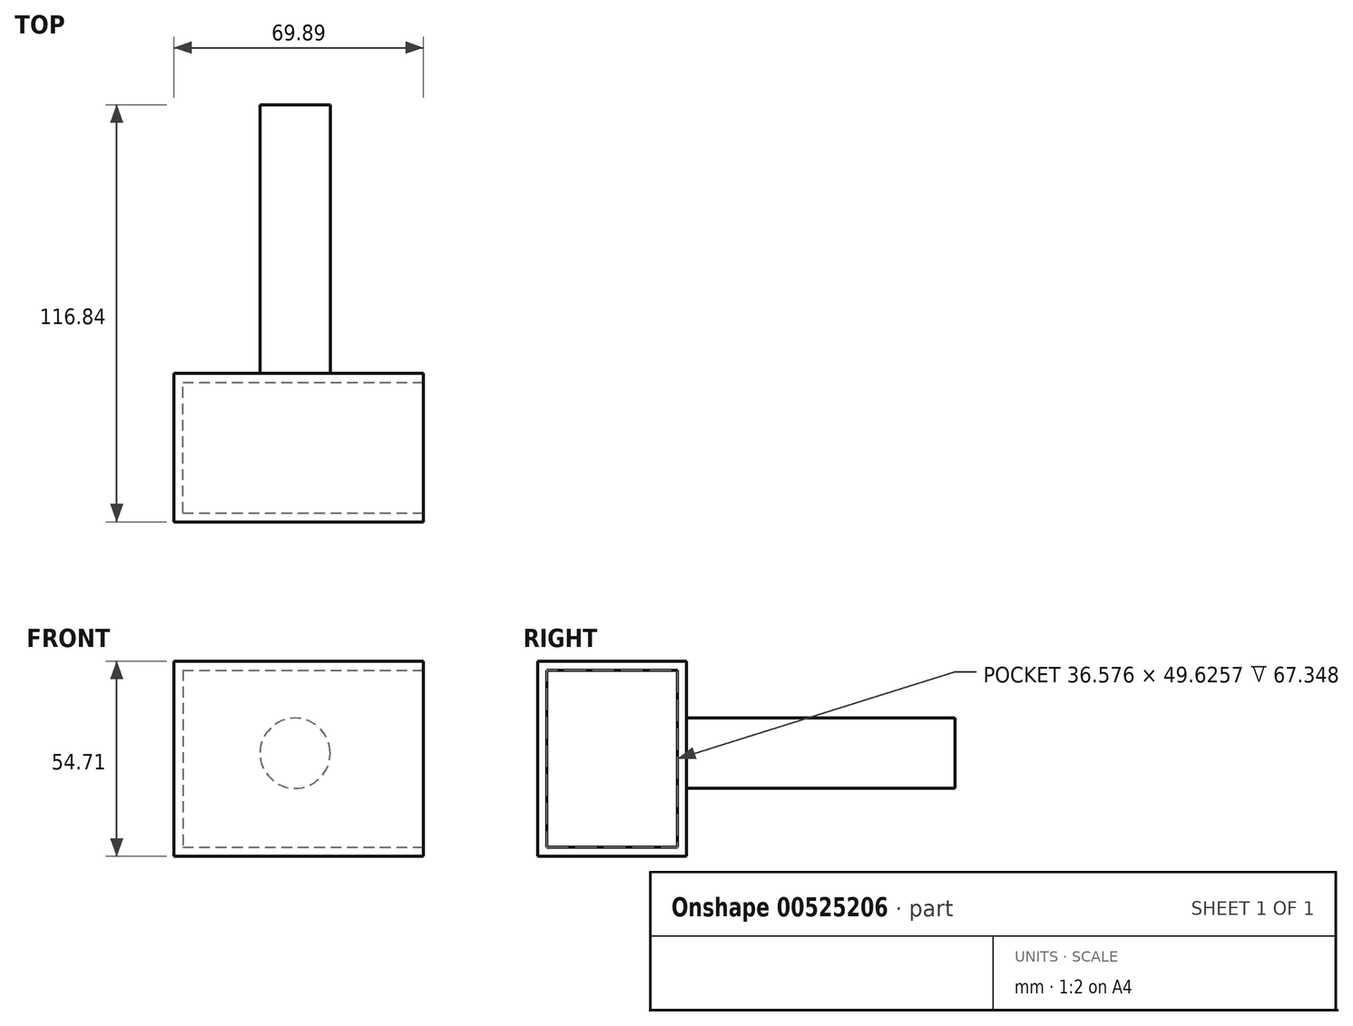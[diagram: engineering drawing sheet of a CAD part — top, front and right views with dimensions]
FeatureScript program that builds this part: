
annotation { "Feature Type Name" : "Feature", "Feature Type Description" : "" }
export const myFeature = defineFeature(function(context is Context, id is Id, definition is map)
    precondition{}
    {
        {
            var Q0;
            Q0=qCreatedBy(makeId("Front.planeOp"),FACE);
            var sketch = newSketch(context, id + "F0", { "sketchPlane" : qUnion([Q0])});
            skLineSegment(sketch, "E0.bottom", {"start": v(-33.98, 25.79) * mm, "end": v(35.9, 25.79) * mm});
            skLineSegment(sketch, "E0.top", {"start": v(-33.98, -28.92) * mm, "end": v(35.9, -28.92) * mm});
            skLineSegment(sketch, "E0.left", {"start": v(-33.98, 25.79) * mm, "end": v(-33.98, -28.92) * mm});
            skLineSegment(sketch, "E0.right", {"start": v(35.9, 25.79) * mm, "end": v(35.9, -28.92) * mm});
            skSolve(sketch);
        }
        {
            var Q0;
            Q0 = qSketchRegion(id + "F0", true);
            extrude(context, id + "F1", {"entities" : qUnion([Q0]), "depth" : 41.66 * mm, "offsetDistance" : 25.4 * mm});
        }
        {
            var Q0;
            Q0=makeQuery(id+"F1.opExtrude","SWEPT_FACE",FACE,{"disambiguationData":[OSD([sQuery(id+"F0.wireOp",EDGE,"E0.right")])]});
            shell(context, id + "F2", {"entities" : qUnion([Q0]), "thickness" : 2.54 * mm});
        }
        {
            var Q0;
            Q0=makeQuery(id+"F1.opExtrude","CAP_FACE",FACE,{"disambiguationData":[OSD([sQuery(id+"F0.wireOp",EDGE,"E0.bottom"),sQuery(id+"F0.wireOp",EDGE,"E0.top"),sQuery(id+"F0.wireOp",EDGE,"E0.left"),sQuery(id+"F0.wireOp",EDGE,"E0.right")])],"isStart":true});
            var sketch = newSketch(context, id + "F3", { "sketchPlane" : qUnion([Q0])});
            skCircle(sketch, "E1", {"center": v(0, 0) * mm, "radius": 9.83 * mm});
            skSolve(sketch);
        }
        {
            var Q0;
            Q0 = qSketchRegion(id + "F3", true);
            extrude(context, id + "F4", {"entities" : qUnion([Q0]), "operationType" : NewBodyOperationType.ADD, "depth" : 75.18 * mm, "offsetDistance" : 25.4 * mm});
        }
    });
